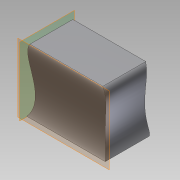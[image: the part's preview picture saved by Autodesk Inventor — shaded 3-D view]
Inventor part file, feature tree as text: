
AUTODESK INVENTOR PART (.ipt)
format: ipt  version: 2011 (Build 150239000, 239)  size: 130,048 bytes
history: native  units: mm
features: other x3, extrude x3, sketch x3, reference x2, projected_geometry x2
ambient origin geometry x8: Origin, YZ Plane, XZ Plane, XY Plane, X Axis, Y Axis, Z Axis, Center Point
feature tree (13):
  other  "Твердое тело1"
  extrude  "Выдавливание1"  Depth=0.2mm
  other  "РабПлоскость1"
  other  "РабПлоскость2"
  extrude  "Выдавливание2"  Depth=0.2mm
  extrude  "Выдавливание3"  Depth=0.2mm
  sketch  "Эскиз1"
  reference  "Ссылка1"
  reference  "Ссылка2"
  sketch  "Эскиз2"
  projected_geometry  "Спроецированная петля1"
  sketch  "Эскиз3"
  projected_geometry  "Спроецированная петля2"
